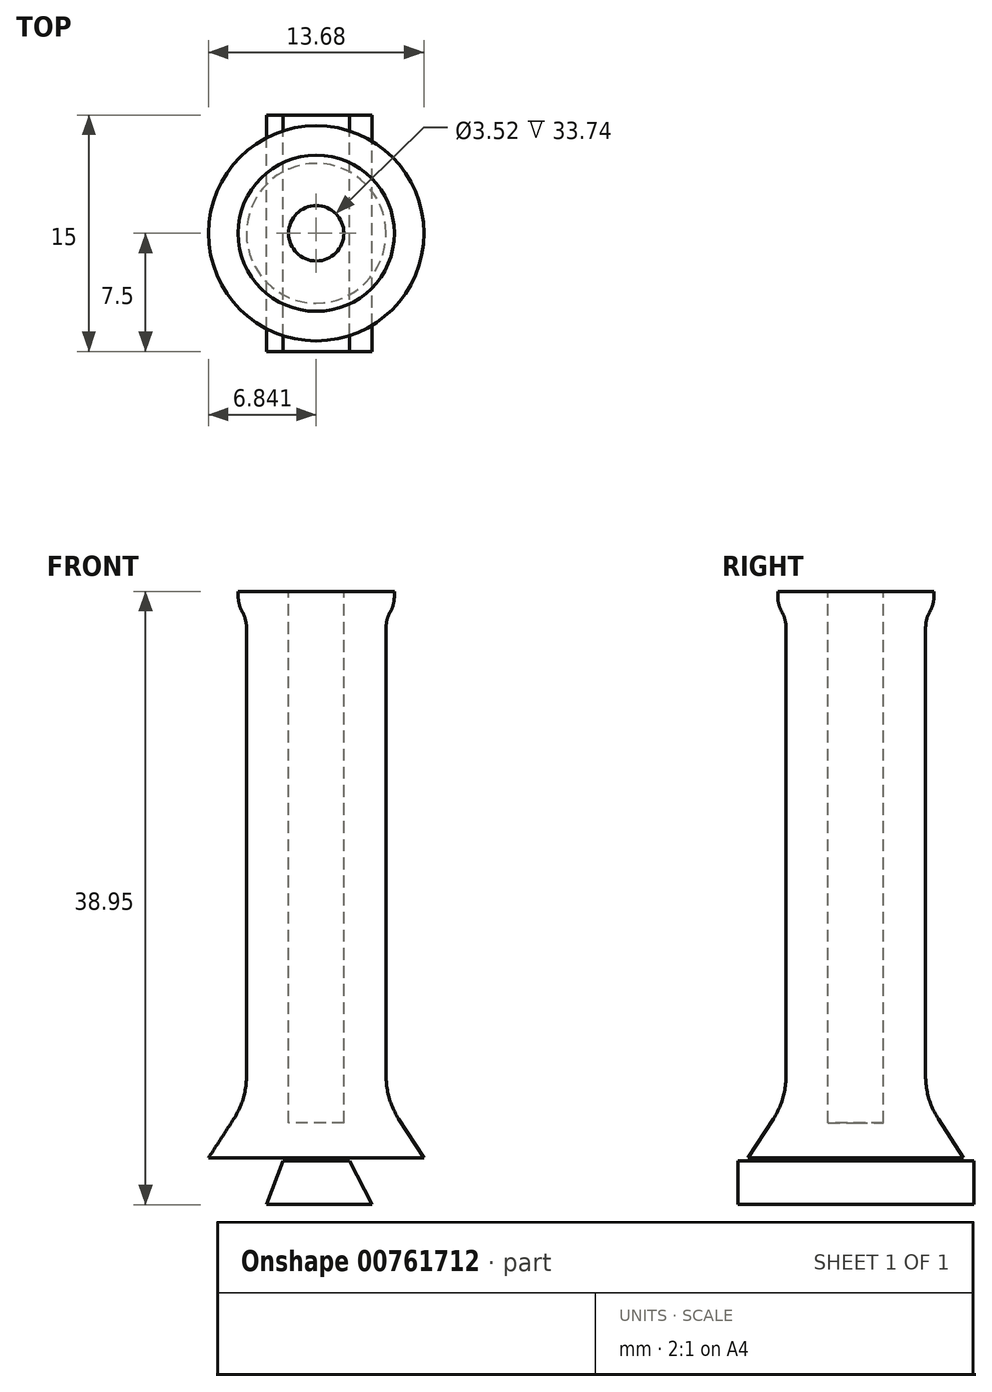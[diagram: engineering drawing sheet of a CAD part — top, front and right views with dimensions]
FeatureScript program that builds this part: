
annotation { "Feature Type Name" : "Feature", "Feature Type Description" : "" }
export const myFeature = defineFeature(function(context is Context, id is Id, definition is map)
    precondition{}
    {
        {
            var Q0;
            Q0=qCreatedBy(makeId("Front.planeOp"),FACE);
            var sketch = newSketch(context, id + "F0", { "sketchPlane" : qUnion([Q0])});
            skLineSegment(sketch, "E0.bottom", {"start": v(5.46, -1.67) * mm, "end": v(-4.74, -1.67) * mm});
            skLineSegment(sketch, "E0.top", {"start": v(7.13, 1.11) * mm, "end": v(1.87, 1.11) * mm});
            skLineSegment(sketch, "E0.left", {"start": v(7.13, -1.67) * mm, "end": v(7.13, 1.11) * mm});
            skLineSegment(sketch, "E0.right", {"start": v(-7.07, -1.67) * mm, "end": v(-7.07, 1.11) * mm});
            skPoint(sketch, "E1.endSnap0", {"position": v(0.03, 1.11) * mm});
            skLineSegment(sketch, "E2", {"start": v(-3.4, -1.67) * mm, "end": v(-2.35, 1.11) * mm});
            skLineSegment(sketch, "E3.MirrorCS", {"start": v(3.28, -1.67) * mm, "end": v(1.87, 1.11) * mm});
            skLineSegment(sketch, "E4.trimOffspring", {"start": v(-2.35, 1.11) * mm, "end": v(-7.07, 1.11) * mm});
            skLineSegment(sketch, "E5", {"start": v(-2.35, 1.11) * mm, "end": v(1.87, 1.11) * mm});
            skLineSegment(sketch, "E6", {"start": v(-7.07, -1.67) * mm, "end": v(7.13, -1.67) * mm});
            skLineSegment(sketch, "E7.bottom", {"start": v(-2.35, 1.11) * mm, "end": v(1.85, 1.11) * mm});
            skLineSegment(sketch, "E7.top", {"start": v(-2.35, 1.31) * mm, "end": v(1.85, 1.31) * mm});
            skLineSegment(sketch, "E7.left", {"start": v(-2.35, 1.11) * mm, "end": v(-2.35, 1.31) * mm});
            skLineSegment(sketch, "E7.right", {"start": v(1.85, 1.11) * mm, "end": v(1.85, 1.31) * mm});
            skPoint(sketch, "E8.orphan", {"position": v(-7.09, 1.31) * mm});
            skLineSegment(sketch, "E9", {"start": v(-0.25, 12.57) * mm, "end": v(-0.25, 1.31) * mm, "construction": true});
            skLineSegment(sketch, "E10", {"start": v(-0.25, 1.31) * mm, "end": v(-7.09, 1.31) * mm});
            skLineSegment(sketch, "E11", {"start": v(-7.09, 1.31) * mm, "end": v(-4.68, 5.02) * mm});
            skLineSegment(sketch, "E12", {"start": v(-4.68, 5.02) * mm, "end": v(-4.68, 35.77) * mm});
            skLineSegment(sketch, "E13", {"start": v(-4.68, 35.77) * mm, "end": v(-5.2, 36.34) * mm});
            skLineSegment(sketch, "E14", {"start": v(-5.2, 36.34) * mm, "end": v(-5.2, 37.28) * mm});
            skLineSegment(sketch, "E15", {"start": v(-5.2, 37.28) * mm, "end": v(-2, 37.28) * mm});
            skLineSegment(sketch, "E16", {"start": v(-0.25, 37.28) * mm, "end": v(-0.25, 1.31) * mm});
            skLineSegment(sketch, "E17", {"start": v(-0.25, 1.31) * mm, "end": v(-0.25, -5.46) * mm, "construction": true});
            skLineSegment(sketch, "E18.bottom", {"start": v(-0.25, 3.54) * mm, "end": v(-2, 3.54) * mm});
            skLineSegment(sketch, "E18.left", {"start": v(-0.25, 3.54) * mm, "end": v(-0.25, 37.28) * mm});
            skLineSegment(sketch, "E18.right", {"start": v(-2, 3.54) * mm, "end": v(-2, 37.28) * mm});
            skSolve(sketch);
        }
        {
            var Q0;
            Q0=makeQuery(id+"F0.imprint","IMPRINT",FACE,{"disambiguationData":[TD([[makeQuery(id+"F0.imprint","IMPRINT",EDGE,{"derivedFrom":sQuery(id+"F0.wireOp",EDGE,"AmVQ8ylY-Ssuw-7Cug-5IGL-YiCEqe24ppy9.top")}),-1.0]])]});
            var Q1;
            Q1=makeQuery(id+"F0.imprint","IMPRINT",FACE,{"disambiguationData":[TD([[makeQuery(id+"F0.imprint","IMPRINT",EDGE,{"derivedFrom":sQuery(id+"F0.wireOp",EDGE,"E7.bottom")}),1.0]])]});
            var Q2;
            {var subQ2=sQuery(id+"F0.wireOp",EDGE,"E2");Q2=makeQuery(id+"F0.imprint","IMPRINT",FACE,{"disambiguationData":[TD([[makeQuery(id+"F0.imprint","IMPRINT",EDGE,{"derivedFrom":subQ2}),-1.0]])]});}
            extrude(context, id + "F1", {"entities" : qUnion([Q0, Q1, Q2]), "endBound" : BoundingType.SYMMETRIC, "depth" : 15 * mm, "offsetDistance" : 25 * mm});
        }
        {
            var Q0;
            {var subQ0=sQuery(id+"F0.wireOp",EDGE,"E11");Q0=makeQuery(id+"F0.imprint","IMPRINT",FACE,{"disambiguationData":[TD([[makeQuery(id+"F0.imprint","IMPRINT",EDGE,{"derivedFrom":subQ0}),-1.0]])]});}
            var Q1;
            Q1=sQuery(id+"F0.wireOp",EDGE,"E17");
            revolve(context, id + "F2", {"operationType" : NewBodyOperationType.ADD, "surfaceOperationType" : NewSurfaceOperationType.NEW, "entities" : qUnion([Q0]), "axis" : qUnion([Q1]), "revolveType" : RevolveType.FULL});
        }
        {
            var Q0;
            Q0=makeQuery(id+"F2.opRevolve","SWEPT_EDGE",EDGE,{"disambiguationData":[OSD([sQuery(id+"F0.wireOp",EDGE,"E11"),sQuery(id+"F0.wireOp",EDGE,"E12")])]});
            fillet(context, id + "F3", {"entities" : qUnion([Q0]), "radius" : 5 * mm, "tangentPropagation" : true, "allowEdgeOverflow" : false});
        }
        {
            var Q0;
            Q0=makeQuery(id+"F2.opRevolve","SWEPT_EDGE",EDGE,{"disambiguationData":[OSD([sQuery(id+"F0.wireOp",EDGE,"E12"),sQuery(id+"F0.wireOp",EDGE,"E13")])]});
            fillet(context, id + "F4", {"entities" : qUnion([Q0]), "radius" : 2 * mm, "tangentPropagation" : true, "allowEdgeOverflow" : false});
        }
        {
            var Q0;
            Q0=makeQuery(id+"F4.opFillet","BLEND_EDGE",EDGE,{"blendedFrom":[makeQuery(id+"F2.opRevolve","SWEPT_EDGE",EDGE,{"disambiguationData":[OSD([sQuery(id+"F0.wireOp",EDGE,"E12"),sQuery(id+"F0.wireOp",EDGE,"E13")])]}),makeQuery(id+"F2.opRevolve","SWEPT_FACE",FACE,{"disambiguationData":[OSD([sQuery(id+"F0.wireOp",EDGE,"E14")])]})],"blendedInto":[makeQuery(id+"F2.opRevolve","SWEPT_FACE",FACE,{"disambiguationData":[OSD([sQuery(id+"F0.wireOp",EDGE,"E14")])]})]});
            fillet(context, id + "F5", {"entities" : qUnion([Q0]), "radius" : 2 * mm, "tangentPropagation" : true, "allowEdgeOverflow" : false});
        }
    });
